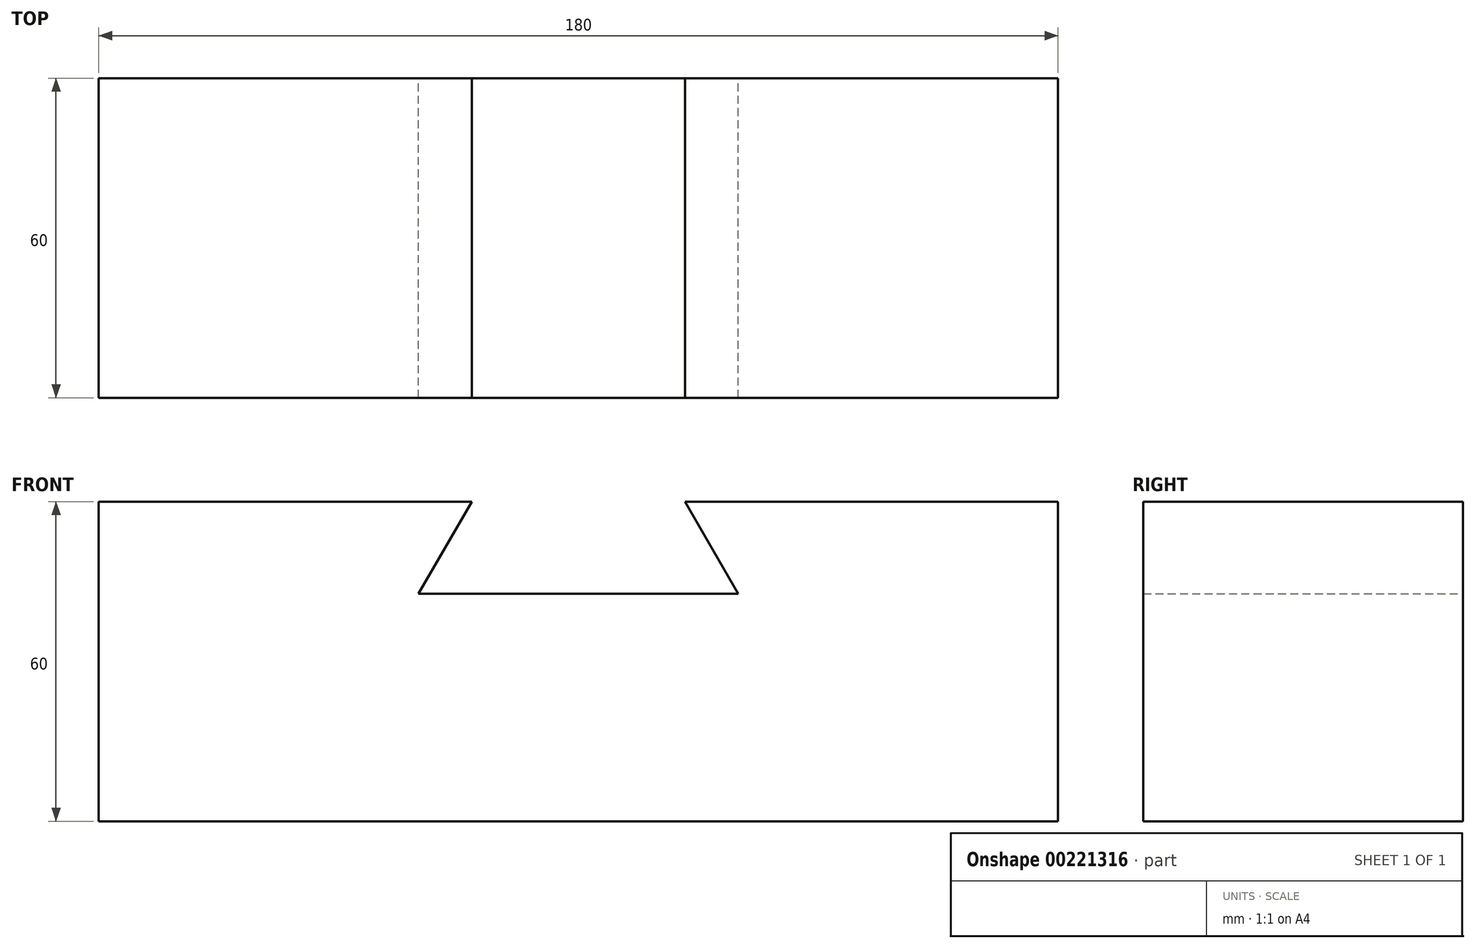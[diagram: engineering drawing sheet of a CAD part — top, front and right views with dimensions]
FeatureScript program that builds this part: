
annotation { "Feature Type Name" : "Feature", "Feature Type Description" : "" }
export const myFeature = defineFeature(function(context is Context, id is Id, definition is map)
    precondition{}
    {
        {
            var Q0;
            Q0=qCreatedBy(makeId("Front.planeOp"),FACE);
            var sketch = newSketch(context, id + "F0", { "sketchPlane" : qUnion([Q0])});
            skLineSegment(sketch, "E0", {"start": v(0, 0) * mm, "end": v(90, 0) * mm});
            skLineSegment(sketch, "E1", {"start": v(90, 0) * mm, "end": v(90, 42.68) * mm, "construction": true});
            skLineSegment(sketch, "E2", {"start": v(90, 42.68) * mm, "end": v(60, 42.68) * mm});
            skLineSegment(sketch, "E3", {"start": v(60, 42.68) * mm, "end": v(70, 60) * mm});
            skLineSegment(sketch, "E4", {"start": v(70, 60) * mm, "end": v(0, 60) * mm});
            skLineSegment(sketch, "E5", {"start": v(0, 60) * mm, "end": v(0, 0) * mm});
            skLineSegment(sketch, "E6.MirrorCS", {"start": v(110, 60) * mm, "end": v(180, 60) * mm});
            skLineSegment(sketch, "E7.MirrorCS", {"start": v(120, 42.68) * mm, "end": v(110, 60) * mm});
            skLineSegment(sketch, "E8.MirrorCS", {"start": v(90, 42.68) * mm, "end": v(120, 42.68) * mm});
            skLineSegment(sketch, "E9.MirrorCS", {"start": v(180, 0) * mm, "end": v(90, 0) * mm});
            skLineSegment(sketch, "E10.MirrorCS", {"start": v(180, 60) * mm, "end": v(180, 0) * mm});
            skSolve(sketch);
        }
        {
            var Q0;
            Q0=makeQuery(id+"F0.imprint","IMPRINT",FACE,{"disambiguationData":[TD([[makeQuery(id+"F0.imprint","IMPRINT",EDGE,{"derivedFrom":sQuery(id+"F0.wireOp",EDGE,"E0")}),1.0]])]});
            extrude(context, id + "F1", {"entities" : qUnion([Q0]), "depth" : 60 * mm});
        }
    });
